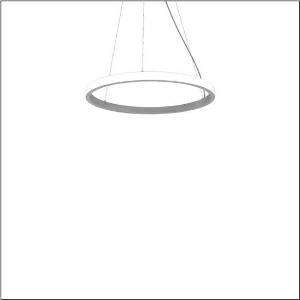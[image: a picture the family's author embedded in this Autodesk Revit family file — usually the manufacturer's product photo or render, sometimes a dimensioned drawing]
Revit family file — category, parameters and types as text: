
# Revit family: silica_r__21_ring-o_5pjbo2d3204a_05ca
name_source: partatom
category: Lighting Fixtures
units: mm (PartAtom-declared; Revit-internal decimal feet)

## family parameters
Cut with Voids When Loaded = No
Host = Face
Light Source = No
Part Type = Normal
Room Calculation Point = No
Round Connector Dimension = Use Diameter
Shared = No

## types (1)
- Silica® 21 Ring-O (1 x LED, 4940 lm, 80 W, 4000K)
    Apparent Load = 80 VA
    CIE Flux Codes = 2 16 49 50 100
    Color Rendering = 80
    Color Temperature = 4000K
    Default Elevation = 1800 mm
    Description = Silica® 21 Ring-O, suspended luminaire, of PMMA, frosted, light emission: outer ring side luminous distribution, primary light characteristic: symmetric, installation type: suspended mounting, LED, rated luminous flux: 4.940lm, luminous efficacy: 62lm/W, light colour: 840, colour temperature: 4000K, control gear: DALI 2, with terminal, 5-pole, mains connection: 230V, AC/DC, 0/50..60Hz, rated input power: 80W, housing, of extruded aluminium section, metallic grey (RAL 9006), diameter: 810mm, ceiling canopy, metallic grey (RAL 9006), protection rating (lamp compartment): IP40, insulation class (complete): insulation class I (protective earthing), certification: CE, impact resistance: IK02, permissible operating ambient temperature: 0..+35°C, packaging unit: 1 piece
    Height = 48 mm  [stored 0.15748 ft]
    Lamp = 1 x LED
    Lamp Light Flux = 4940 lm
    Lamp Power = 80 W
    Lamp count = 1
    Length = 810 mm
    Luminous efficacy = 62 lm/W
    Manufacturer = Siteco
    ModVariant = No
    Model = 5PJBO2D3204A
    Mounting Place = Ceiling
    Mounting Type = Pendant
    Number of Poles = 1
    OnlyDefault = Yes
    Power Factor = 1
    Product Name = Silica® 21 Ring-O
    Product group = suspended luminaire
    ProductGroupID = 905
    Protection Class = Protection class I
    Protection Degree = IP 40
    RLX_Detail_Level = 1
    RLX_Emergency_Light_Flux = 0 lm
    RLX_Emergency_Type = 0
    RLX_Emergency_Type_DB = No
    RlxData = <blob elided: 13069 chars, md5=55f2f3db>
    Socket = socket
    Standby Power = 0 W
    System Light Flux = 4940 lm
    System Power = 80 W
    Type Comments = Product without accessories
    Type Image = l_1251760.jpg
    URL = http://relux.com
    VarID = ---
    Voltage = 0 V
    Weight = 0.00 kg
    Width = 0 mm  [stored 0 ft]

note: [stored X ft] marks values corroborated as IEEE doubles in the binary element streams (Revit-internal decimal feet)

## geometry (parser evidence)
native form markers: Sweep x11
no freeform markers — native parametric forms only
